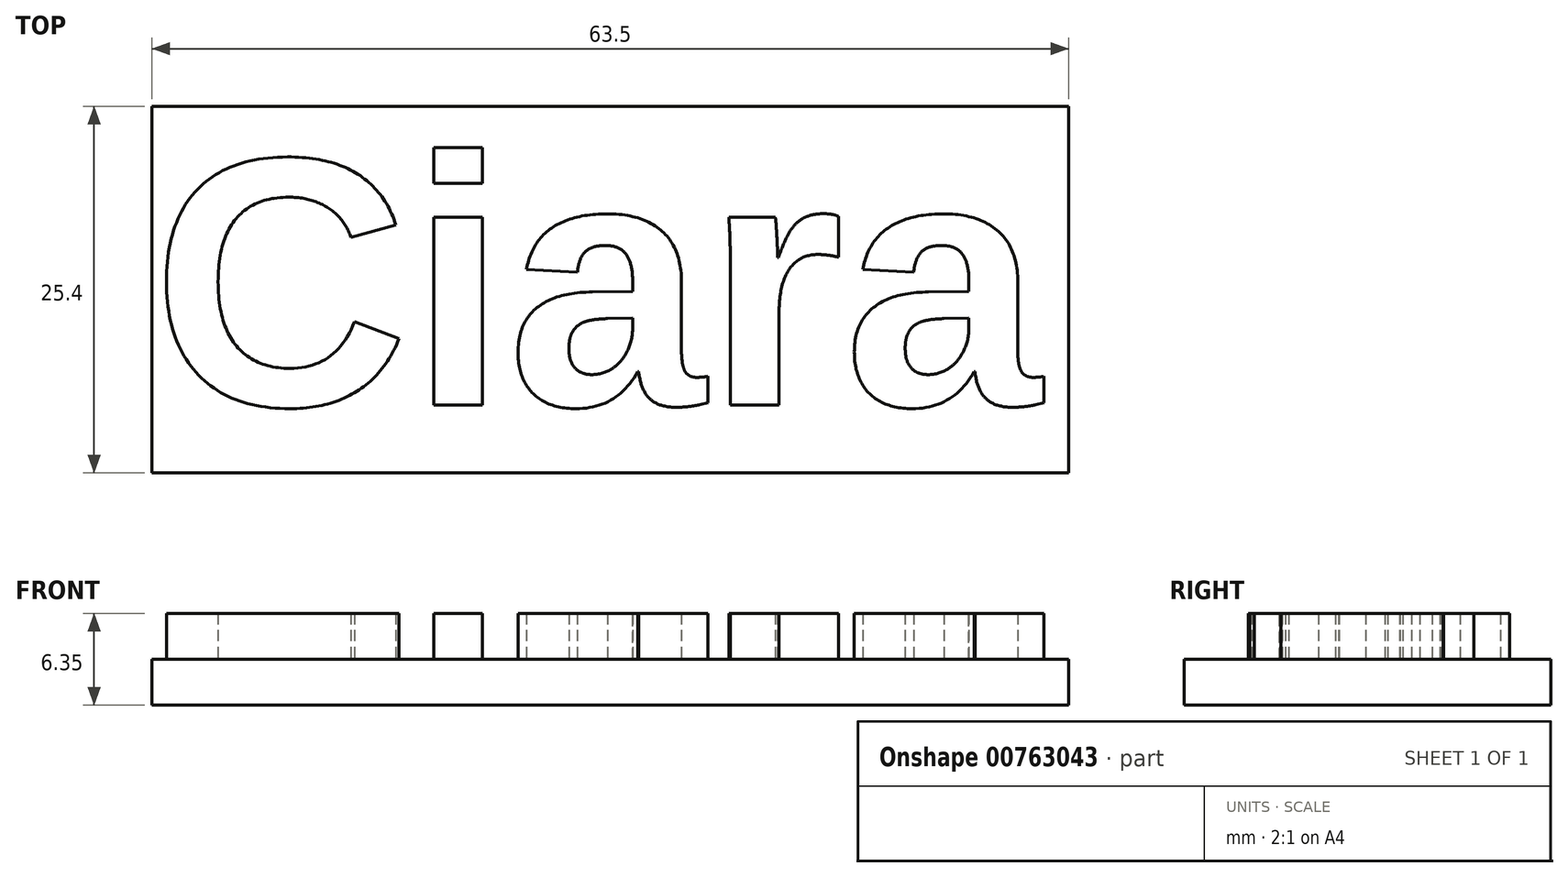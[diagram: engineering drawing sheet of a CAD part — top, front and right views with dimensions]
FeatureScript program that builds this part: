
annotation { "Feature Type Name" : "Feature", "Feature Type Description" : "" }
export const myFeature = defineFeature(function(context is Context, id is Id, definition is map)
    precondition{}
    {
        {
            var Q0;
            Q0=qCreatedBy(makeId("Top.planeOp"),FACE);
            var sketch = newSketch(context, id + "F0", { "sketchPlane" : qUnion([Q0])});
            skLineSegment(sketch, "E0.bottom", {"start": v(0, 0) * mm, "end": v(63.5, 0) * mm});
            skLineSegment(sketch, "E0.top", {"start": v(0, 25.4) * mm, "end": v(63.5, 25.4) * mm});
            skLineSegment(sketch, "E0.left", {"start": v(0, 0) * mm, "end": v(0, 25.4) * mm});
            skLineSegment(sketch, "E0.right", {"start": v(63.5, 0) * mm, "end": v(63.5, 25.4) * mm});
            skSolve(sketch);
        }
        {
            var Q0;
            Q0=makeQuery(id+"F0.imprint","IMPRINT",FACE,{"disambiguationData":[TD([[makeQuery(id+"F0.imprint","IMPRINT",EDGE,{"derivedFrom":sQuery(id+"F0.wireOp",EDGE,"E0.bottom")}),1.0]])]});
            extrude(context, id + "F1", {"entities" : qUnion([Q0]), "depth" : 3.17 * mm, "offsetDistance" : 25.4 * mm});
        }
        {
            var Q0;
            Q0=qCreatedBy(makeId("Top.planeOp"),FACE);
            var sketch = newSketch(context, id + "F2", { "sketchPlane" : qUnion([Q0])});
            skText(sketch, "E1", { "text": "Ciara", "fontName": "Arimo-Bold.ttf"});
            const initialGuessF2  = {"E1": [0, 0.00469, 1, 0, 0.01774]};
            skSetInitialGuess(sketch, initialGuessF2);
            skSolve(sketch);
        }
        {
            var Q0;
            Q0 = qSketchRegion(id + "F2", true);
            extrude(context, id + "F3", {"entities" : qUnion([Q0]), "operationType" : NewBodyOperationType.ADD, "depth" : 6.35 * mm, "offsetDistance" : 25.4 * mm});
        }
    });
